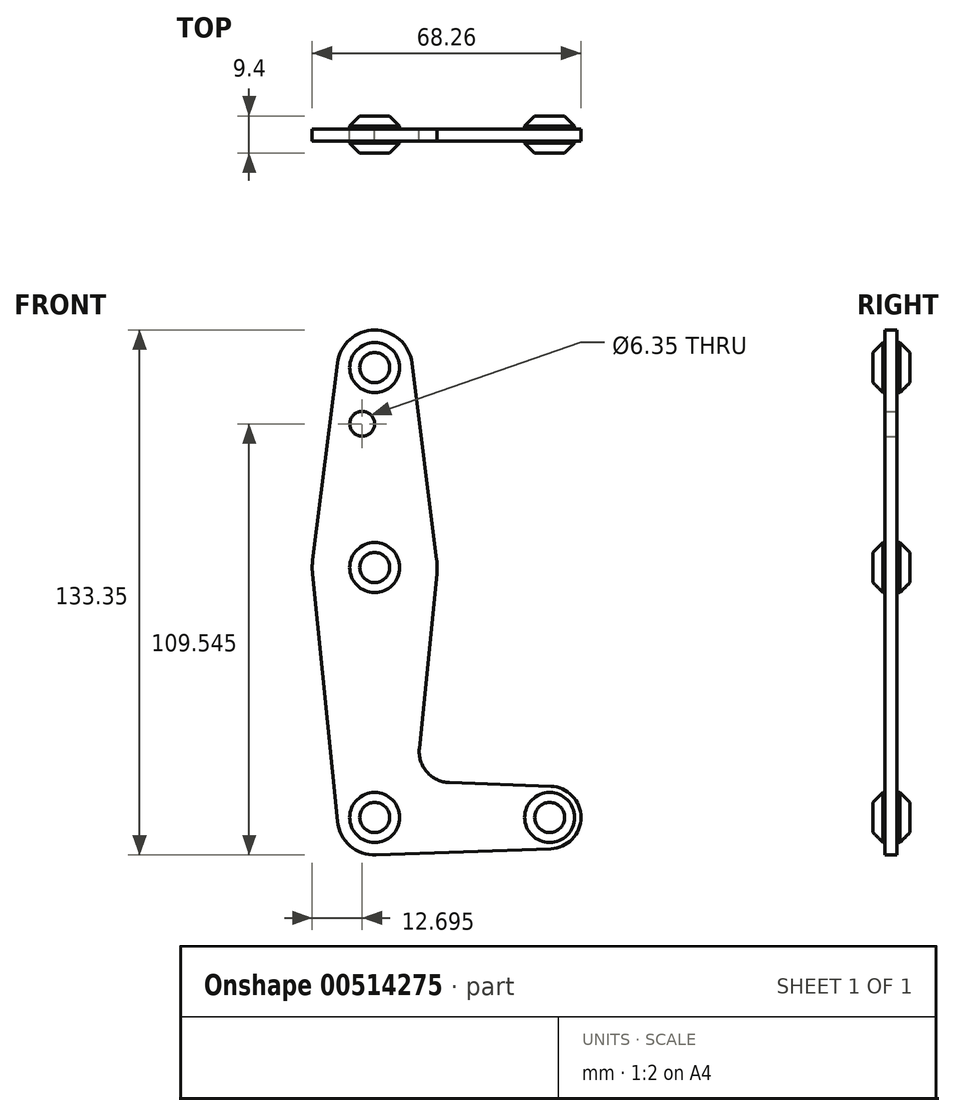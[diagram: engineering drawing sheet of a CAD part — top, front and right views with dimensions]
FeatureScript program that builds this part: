
annotation { "Feature Type Name" : "Feature", "Feature Type Description" : "" }
export const myFeature = defineFeature(function(context is Context, id is Id, definition is map)
    precondition{}
    {
        {
            var Q0;
            Q0=qCreatedBy(makeId("Front.planeOp"),FACE);
            var sketch = newSketch(context, id + "F0", { "sketchPlane" : qUnion([Q0])});
            skLineSegment(sketch, "E0", {"start": v(0, 0) * mm, "end": v(0, 114.3) * mm, "construction": true});
            skLineSegment(sketch, "E1", {"start": v(0, 0) * mm, "end": v(44.45, 0) * mm, "construction": true});
            skCircle(sketch, "E2", {"center": v(0, 114.3) * mm, "radius": 9.53 * mm});
            skCircle(sketch, "E3", {"center": v(0, 63.5) * mm, "radius": 15.88 * mm});
            skCircle(sketch, "E4", {"center": v(0, 0) * mm, "radius": 9.53 * mm});
            skCircle(sketch, "E5", {"center": v(44.45, 0) * mm, "radius": 7.94 * mm});
            skLineSegment(sketch, "E6", {"start": v(-9.45, 115.5) * mm, "end": v(-15.75, 65.48) * mm});
            skLineSegment(sketch, "E7", {"start": v(9.45, 115.5) * mm, "end": v(15.75, 65.48) * mm});
            skLineSegment(sketch, "E8", {"start": v(44.73, 7.93) * mm, "end": v(18.97, 8.85) * mm});
            skLineSegment(sketch, "E9", {"start": v(44.73, -7.93) * mm, "end": v(0, -9.53) * mm});
            skLineSegment(sketch, "E10", {"start": v(15.8, 61.91) * mm, "end": v(11.34, 17.6) * mm});
            skLineSegment(sketch, "E11", {"start": v(-15.8, 61.91) * mm, "end": v(-9.48, -0.95) * mm});
            skPoint(sketch, "E12.newPointB", {"position": v(0, 9.53) * mm});
            skArc(sketch, "E12.filletArc", {"start": v(11.34, 17.6) * mm, "mid": v(13.26, 11.57) * mm, "end": v(18.97, 8.85) * mm});
            skCircle(sketch, "E13", {"center": v(0, 114.3) * mm, "radius": 3.18 * mm});
            skCircle(sketch, "E14", {"center": v(-3.18, 100.03) * mm, "radius": 3.18 * mm});
            skCircle(sketch, "E15", {"center": v(0, 63.5) * mm, "radius": 3.18 * mm});
            skCircle(sketch, "E16", {"center": v(0, 0) * mm, "radius": 3.18 * mm});
            skCircle(sketch, "E17", {"center": v(44.45, 0) * mm, "radius": 3.18 * mm});
            skSolve(sketch);
        }
        {
            var Q0;
            Q0 = qSketchRegion(id + "F0", true);
            extrude(context, id + "F1", {"entities" : qUnion([Q0]), "depth" : 3.05 * mm});
        }
        {
            var Q0;
            Q0=makeQuery(id+"F1.opExtrude","CAP_FACE",FACE,{"disambiguationData":[OSD([sQuery(id+"F0.wireOp",EDGE,"E2"),sQuery(id+"F0.wireOp",EDGE,"E3"),sQuery(id+"F0.wireOp",EDGE,"E4"),sQuery(id+"F0.wireOp",EDGE,"E5"),sQuery(id+"F0.wireOp",EDGE,"E6"),sQuery(id+"F0.wireOp",EDGE,"E7"),sQuery(id+"F0.wireOp",EDGE,"E8"),sQuery(id+"F0.wireOp",EDGE,"E9"),sQuery(id+"F0.wireOp",EDGE,"E10"),sQuery(id+"F0.wireOp",EDGE,"E11"),sQuery(id+"F0.wireOp",EDGE,"E12.filletArc"),sQuery(id+"F0.wireOp",EDGE,"E13"),sQuery(id+"F0.wireOp",EDGE,"E14"),sQuery(id+"F0.wireOp",EDGE,"E15"),sQuery(id+"F0.wireOp",EDGE,"E16"),sQuery(id+"F0.wireOp",EDGE,"E17")])],"isStart":false});
            var sketch = newSketch(context, id + "F2", { "sketchPlane" : qUnion([Q0])});
            skCircle(sketch, "E18", {"center": v(0, 114.3) * mm, "radius": 6.35 * mm});
            skCircle(sketch, "E19", {"center": v(0, 63.5) * mm, "radius": 6.35 * mm});
            skCircle(sketch, "E20", {"center": v(44.45, 0) * mm, "radius": 6.35 * mm});
            skCircle(sketch, "E21", {"center": v(0, 0) * mm, "radius": 6.35 * mm});
            skSolve(sketch);
        }
        {
            var Q0;
            Q0 = qSketchRegion(id + "F2", true);
            extrude(context, id + "F3", {"entities" : qUnion([Q0]), "operationType" : NewBodyOperationType.ADD, "depth" : 3.05 * mm, "hasSecondDirection" : true, "secondDirectionOppositeDirection" : true, "secondDirectionDepth" : 6.35 * mm});
        }
        {
            var Q0;
            Q0=makeQuery(id+"F3.opExtrude","CAP_EDGE",EDGE,{"disambiguationData":[OSD([sQuery(id+"F2.wireOp",EDGE,"E18")])],"isStart":true});
            var Q1;
            Q1=makeQuery(id+"F3.opExtrude","CAP_EDGE",EDGE,{"disambiguationData":[OSD([sQuery(id+"F2.wireOp",EDGE,"E18")])],"isStart":false});
            var Q2;
            Q2=makeQuery(id+"F3.opExtrude","CAP_EDGE",EDGE,{"disambiguationData":[OSD([sQuery(id+"F2.wireOp",EDGE,"E19")])],"isStart":true});
            var Q3;
            Q3=makeQuery(id+"F3.opExtrude","CAP_EDGE",EDGE,{"disambiguationData":[OSD([sQuery(id+"F2.wireOp",EDGE,"E21")])],"isStart":true});
            var Q4;
            Q4=makeQuery(id+"F3.opExtrude","CAP_EDGE",EDGE,{"disambiguationData":[OSD([sQuery(id+"F2.wireOp",EDGE,"E20")])],"isStart":true});
            var Q5;
            Q5=makeQuery(id+"F3.opExtrude","CAP_EDGE",EDGE,{"disambiguationData":[OSD([sQuery(id+"F2.wireOp",EDGE,"E20")])],"isStart":false});
            var Q6;
            Q6=makeQuery(id+"F3.opExtrude","CAP_EDGE",EDGE,{"disambiguationData":[OSD([sQuery(id+"F2.wireOp",EDGE,"E19")])],"isStart":false});
            var Q7;
            Q7=makeQuery(id+"F3.opExtrude","CAP_EDGE",EDGE,{"disambiguationData":[OSD([sQuery(id+"F2.wireOp",EDGE,"E21")])],"isStart":false});
            chamfer(context, id + "F4", {"entities" : qUnion([Q0, Q1, Q2, Q3, Q4, Q5, Q6, Q7]), "width" : 2.54 * mm, "tangentPropagation" : true});
        }
    });
